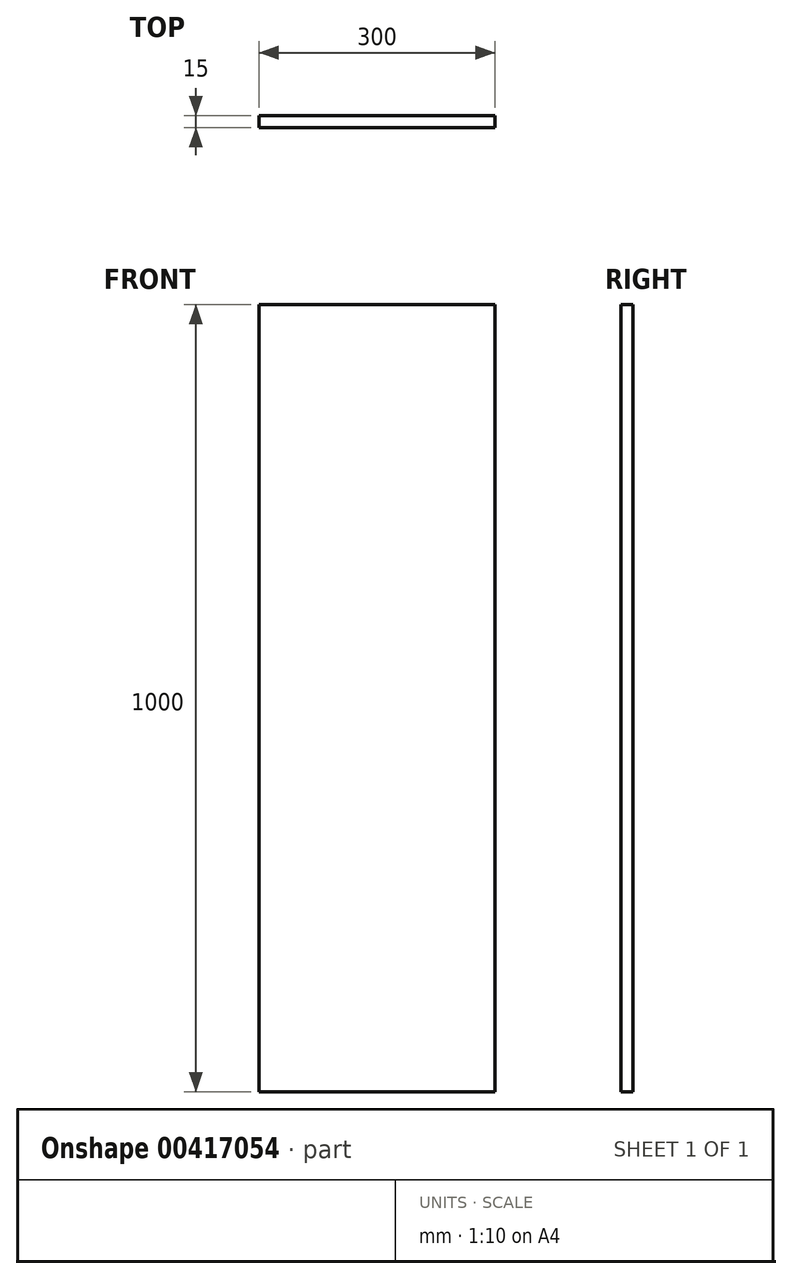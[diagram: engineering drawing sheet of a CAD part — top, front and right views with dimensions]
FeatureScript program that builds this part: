
annotation { "Feature Type Name" : "Feature", "Feature Type Description" : "" }
export const myFeature = defineFeature(function(context is Context, id is Id, definition is map)
    precondition{}
    {
        {
            var Q0;
            Q0=qCreatedBy(makeId("Front.planeOp"),FACE);
            var sketch = newSketch(context, id + "F0", { "sketchPlane" : qUnion([Q0])});
            skLineSegment(sketch, "E0", {"start": v(150, 0) * mm, "end": v(150, 500) * mm});
            skLineSegment(sketch, "E1", {"start": v(150, 500) * mm, "end": v(-150, 500) * mm});
            skLineSegment(sketch, "E2", {"start": v(-150, 500) * mm, "end": v(-150, -500) * mm});
            skLineSegment(sketch, "E3", {"start": v(-150, -500) * mm, "end": v(150, -500) * mm});
            skLineSegment(sketch, "E4", {"start": v(150, -500) * mm, "end": v(150, 0) * mm});
            skSolve(sketch);
        }
        {
            var Q0;
            Q0=makeQuery(id+"F0.imprint","IMPRINT",FACE,{"disambiguationData":[TD([[makeQuery(id+"F0.imprint","IMPRINT",EDGE,{"derivedFrom":sQuery(id+"F0.wireOp",EDGE,"E0")}),1.0]])]});
            extrude(context, id + "F1", {"entities" : qUnion([Q0]), "depth" : 15 * mm, "offsetDistance" : 25 * mm});
        }
    });
